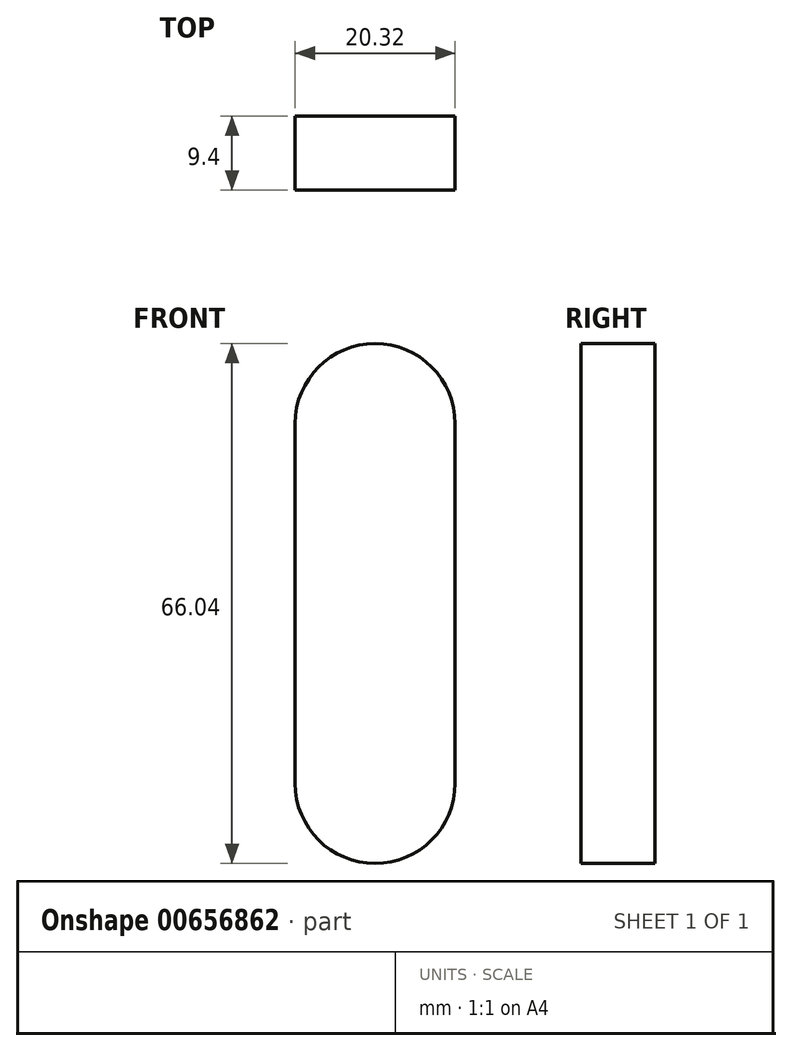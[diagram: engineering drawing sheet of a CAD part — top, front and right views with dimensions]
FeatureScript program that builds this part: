
annotation { "Feature Type Name" : "Feature", "Feature Type Description" : "" }
export const myFeature = defineFeature(function(context is Context, id is Id, definition is map)
    precondition{}
    {
        {
            var Q0;
            Q0=qCreatedBy(makeId("Front.planeOp"),FACE);
            var sketch = newSketch(context, id + "F0", { "sketchPlane" : qUnion([Q0])});
            skLineSegment(sketch, "E0", {"start": v(-20.74, -16.52) * mm, "end": v(-20.74, -16.52) * mm});
            skLineSegment(sketch, "E1", {"start": v(-30.9, -6.36) * mm, "end": v(-30.9, 16.5) * mm});
            skLineSegment(sketch, "E2.MirrorCS", {"start": v(-10.58, -6.36) * mm, "end": v(-10.58, 16.5) * mm});
            skLineSegment(sketch, "E3.MirrorCS", {"start": v(-20.74, 49.52) * mm, "end": v(-20.74, 49.52) * mm});
            skLineSegment(sketch, "E4.MirrorCS", {"start": v(-30.9, 39.36) * mm, "end": v(-30.9, 16.5) * mm});
            skLineSegment(sketch, "E5.MirrorCS", {"start": v(-10.58, 39.36) * mm, "end": v(-10.58, 16.5) * mm});
            skPoint(sketch, "E6.MirrorCS.end.orphan", {"position": v(-20.74, 16.5) * mm});
            skPoint(sketch, "E7.visualSharp", {"position": v(-30.9, -16.52) * mm});
            skArc(sketch, "E7.filletArc", {"start": v(-30.9, -6.36) * mm, "mid": v(-27.92, -13.54) * mm, "end": v(-20.74, -16.52) * mm});
            skPoint(sketch, "E8.visualSharp", {"position": v(-10.58, -16.52) * mm});
            skArc(sketch, "E8.filletArc", {"start": v(-20.74, -16.52) * mm, "mid": v(-13.56, -13.54) * mm, "end": v(-10.58, -6.36) * mm});
            skPoint(sketch, "E9.visualSharp", {"position": v(-30.9, 49.52) * mm});
            skArc(sketch, "E9.filletArc", {"start": v(-20.74, 49.52) * mm, "mid": v(-27.92, 46.54) * mm, "end": v(-30.9, 39.36) * mm});
            skPoint(sketch, "E10.visualSharp", {"position": v(-10.58, 49.52) * mm});
            skArc(sketch, "E10.filletArc", {"start": v(-10.58, 39.36) * mm, "mid": v(-13.56, 46.54) * mm, "end": v(-20.74, 49.52) * mm});
            skSolve(sketch);
        }
        {
            var Q0;
            Q0 = qSketchRegion(id + "F0", true);
            extrude(context, id + "F1", {"entities" : qUnion([Q0]), "endBound" : BoundingType.SYMMETRIC, "depth" : 9.4 * mm, "offsetDistance" : 25.4 * mm});
        }
    });
